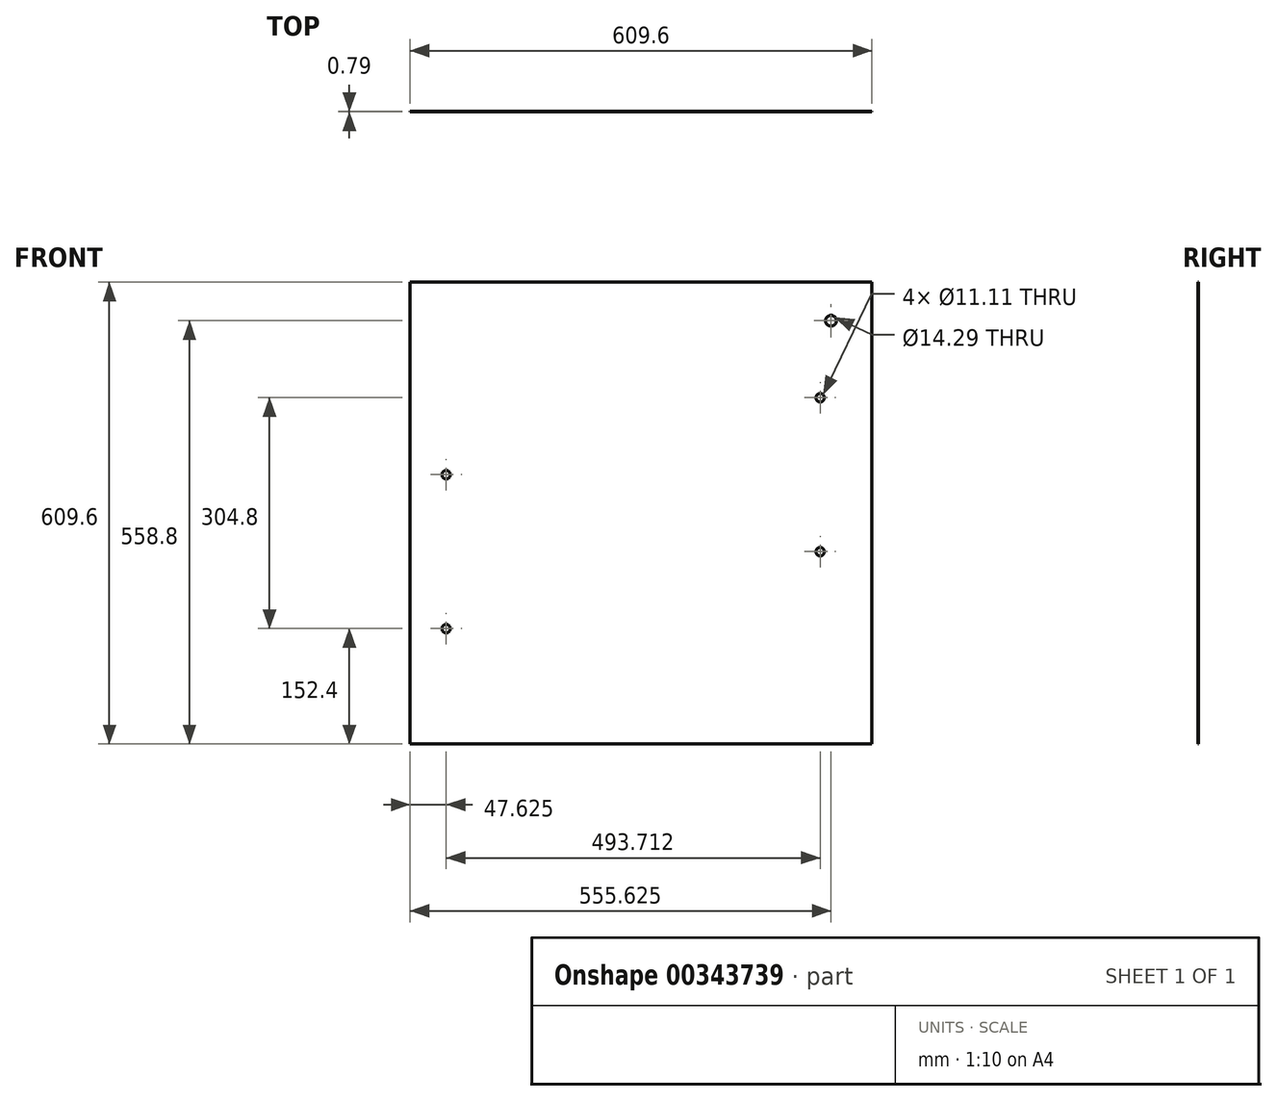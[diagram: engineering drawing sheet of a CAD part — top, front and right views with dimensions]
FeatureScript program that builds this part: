
annotation { "Feature Type Name" : "Feature", "Feature Type Description" : "" }
export const myFeature = defineFeature(function(context is Context, id is Id, definition is map)
    precondition{}
    {
        {
            var Q0;
            Q0=qCreatedBy(makeId("Front.planeOp"),FACE);
            var sketch = newSketch(context, id + "F0", { "sketchPlane" : qUnion([Q0])});
            skLineSegment(sketch, "E0.bottom", {"start": v(0, 0) * mm, "end": v(609.6, 0) * mm});
            skLineSegment(sketch, "E0.top", {"start": v(0, 609.6) * mm, "end": v(609.6, 609.6) * mm});
            skLineSegment(sketch, "E0.left", {"start": v(0, 0) * mm, "end": v(0, 609.6) * mm});
            skLineSegment(sketch, "E0.right", {"start": v(609.6, 0) * mm, "end": v(609.6, 609.6) * mm});
            skSolve(sketch);
        }
        {
            var Q0;
            Q0=makeQuery(id+"F0.imprint","IMPRINT",FACE,{"disambiguationData":[TD([[makeQuery(id+"F0.imprint","IMPRINT",EDGE,{"derivedFrom":sQuery(id+"F0.wireOp",EDGE,"E0.top")}),-1.0]])]});
            extrude(context, id + "F1", {"entities" : qUnion([Q0]), "depth" : 0.8 * mm});
        }
        {
            var Q0;
            Q0=makeQuery(id+"F1.opExtrude","CAP_FACE",FACE,{"disambiguationData":[OSD([sQuery(id+"F0.wireOp",EDGE,"E0.bottom"),sQuery(id+"F0.wireOp",EDGE,"E0.top"),sQuery(id+"F0.wireOp",EDGE,"E0.left"),sQuery(id+"F0.wireOp",EDGE,"E0.right")])],"isStart":false});
            var sketch = newSketch(context, id + "F2", { "sketchPlane" : qUnion([Q0])});
            skCircle(sketch, "E1", {"center": v(47.63, 152.4) * mm, "radius": 5.56 * mm});
            skCircle(sketch, "E2", {"center": v(47.62, 355.6) * mm, "radius": 5.56 * mm});
            skCircle(sketch, "E3", {"center": v(541.34, 457.2) * mm, "radius": 5.56 * mm});
            skCircle(sketch, "E4", {"center": v(541.34, 254) * mm, "radius": 5.56 * mm});
            skSolve(sketch);
        }
        {
            var Q0;
            Q0=makeQuery(id+"F2.imprint","IMPRINT",FACE,{"disambiguationData":[TD([[makeQuery(id+"F2.imprint","IMPRINT",EDGE,{"derivedFrom":sQuery(id+"F2.wireOp",EDGE,"E2")}),1.0]])]});
            var Q1;
            Q1=makeQuery(id+"F2.imprint","IMPRINT",FACE,{"disambiguationData":[TD([[makeQuery(id+"F2.imprint","IMPRINT",EDGE,{"derivedFrom":sQuery(id+"F2.wireOp",EDGE,"E1")}),1.0]])]});
            var Q2;
            Q2=makeQuery(id+"F2.imprint","IMPRINT",FACE,{"disambiguationData":[TD([[makeQuery(id+"F2.imprint","IMPRINT",EDGE,{"derivedFrom":sQuery(id+"F2.wireOp",EDGE,"E4")}),1.0]])]});
            var Q3;
            Q3=makeQuery(id+"F2.imprint","IMPRINT",FACE,{"disambiguationData":[TD([[makeQuery(id+"F2.imprint","IMPRINT",EDGE,{"derivedFrom":sQuery(id+"F2.wireOp",EDGE,"E3")}),1.0]])]});
            extrude(context, id + "F3", {"entities" : qUnion([Q0, Q1, Q2, Q3]), "operationType" : NewBodyOperationType.REMOVE, "oppositeDirection" : true, "depth" : 25.4 * mm});
        }
        {
            var Q0;
            Q0=makeQuery(id+"F1.opExtrude","CAP_FACE",FACE,{"disambiguationData":[OSD([sQuery(id+"F0.wireOp",EDGE,"E0.bottom"),sQuery(id+"F0.wireOp",EDGE,"E0.top"),sQuery(id+"F0.wireOp",EDGE,"E0.left"),sQuery(id+"F0.wireOp",EDGE,"E0.right")])],"isStart":false});
            var sketch = newSketch(context, id + "F4", { "sketchPlane" : qUnion([Q0])});
            skLineSegment(sketch, "E5", {"start": v(568.32, 609.6) * mm, "end": v(568.33, 0) * mm, "construction": true});
            skCircle(sketch, "E6", {"center": v(555.62, 558.8) * mm, "radius": 7.14 * mm});
            skSolve(sketch);
        }
        {
            var Q0;
            Q0=makeQuery(id+"F4.imprint","IMPRINT",FACE,{"disambiguationData":[TD([[makeQuery(id+"F4.imprint","IMPRINT",EDGE,{"derivedFrom":sQuery(id+"F4.wireOp",EDGE,"E6")}),1.0]])]});
            extrude(context, id + "F5", {"entities" : qUnion([Q0]), "operationType" : NewBodyOperationType.REMOVE, "oppositeDirection" : true, "depth" : 25.4 * mm});
        }
    });
